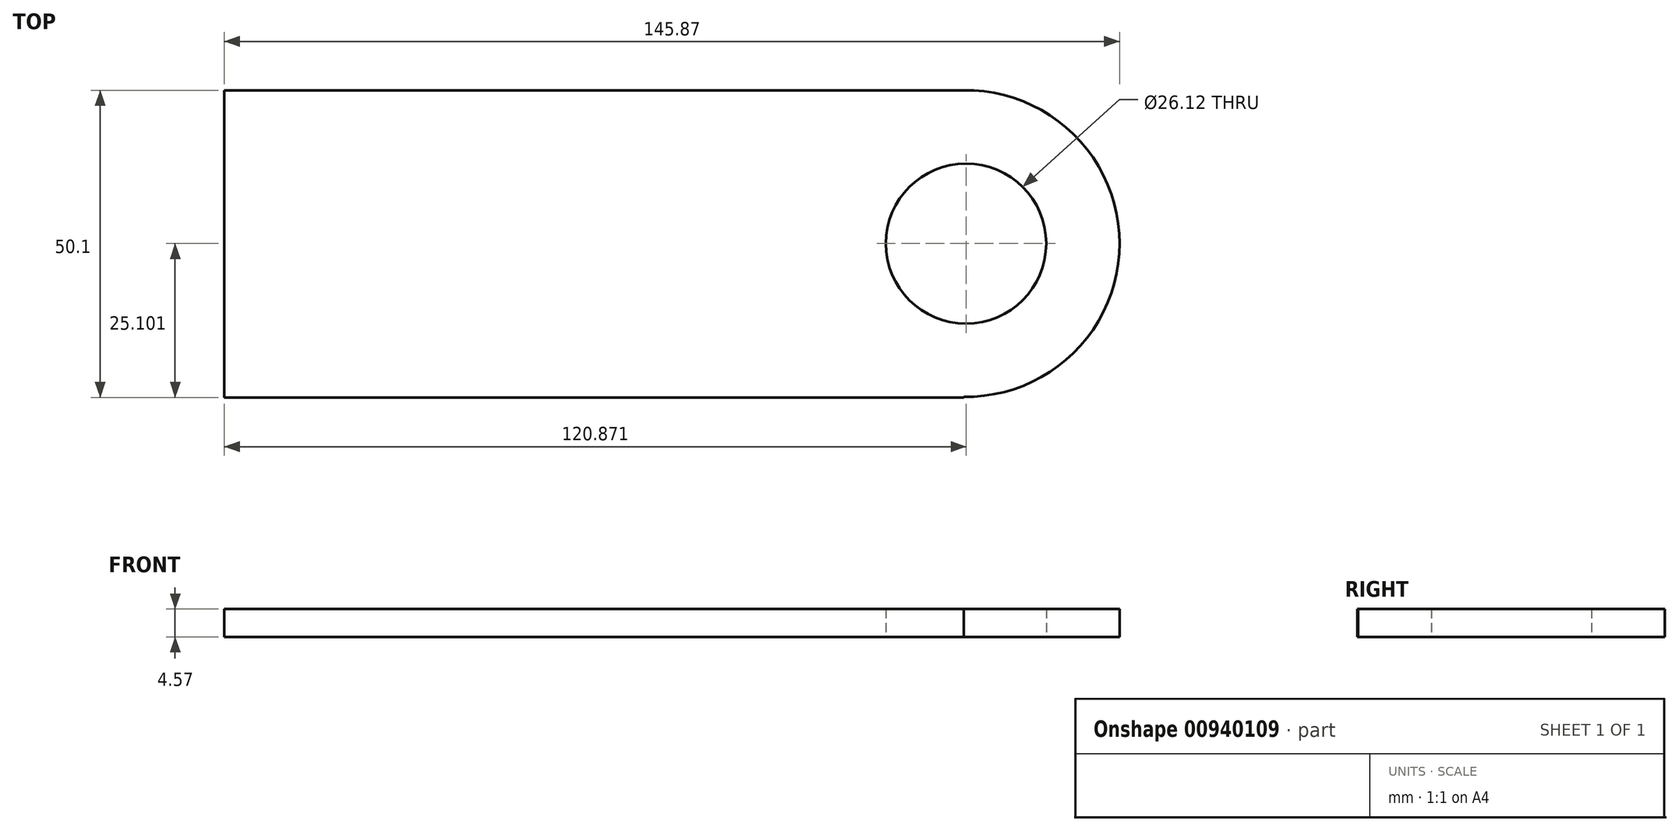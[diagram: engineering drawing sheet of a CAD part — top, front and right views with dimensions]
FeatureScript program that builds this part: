
annotation { "Feature Type Name" : "Feature", "Feature Type Description" : "" }
export const myFeature = defineFeature(function(context is Context, id is Id, definition is map)
    precondition{}
    {
        {
            var Q0;
            Q0=qCreatedBy(makeId("Top.planeOp"),FACE);
            var sketch = newSketch(context, id + "F0", { "sketchPlane" : qUnion([Q0])});
            skCircle(sketch, "E0", {"center": v(-9.74, 47.99) * mm, "radius": 25 * mm});
            skLineSegment(sketch, "E1.bottom", {"start": v(-34.74, 47.59) * mm, "end": v(15.36, 47.59) * mm});
            skLineSegment(sketch, "E1.top", {"start": v(-34.74, -72.88) * mm, "end": v(15.36, -72.88) * mm});
            skLineSegment(sketch, "E1.left", {"start": v(-34.74, 47.59) * mm, "end": v(-34.74, -72.88) * mm});
            skLineSegment(sketch, "E1.right", {"start": v(15.36, 47.59) * mm, "end": v(15.36, -72.88) * mm});
            skCircle(sketch, "E2", {"center": v(-9.74, 47.99) * mm, "radius": 13.06 * mm});
            skSolve(sketch);
        }
        {
            var Q0;
            Q0 = qSketchRegion(id + "F0", true);
            extrude(context, id + "F1", {"entities" : qUnion([Q0]), "depth" : 4.57 * mm, "offsetDistance" : 25.4 * mm});
        }
        {
            var Q0;
            Q0=makeQuery(id+"F1.opExtrude","SWEPT_BODY",BODY,{"disambiguationData":[OSD([sQuery(id+"F0.wireOp",EDGE,"E0"),sQuery(id+"F0.wireOp",EDGE,"E1.bottom"),sQuery(id+"F0.wireOp",EDGE,"E1.top"),sQuery(id+"F0.wireOp",EDGE,"E1.left"),sQuery(id+"F0.wireOp",EDGE,"E1.right"),sQuery(id+"F0.wireOp",EDGE,"E2")])]});
            var Q1;
            Q1=makeQuery(id+"F1.opExtrude","SWEPT_EDGE",EDGE,{"disambiguationData":[OSD([sQuery(id+"F0.wireOp",EDGE,"E0"),sQuery(id+"F0.wireOp",EDGE,"E1.bottom"),sQuery(id+"F0.wireOp",EDGE,"E1.left")])]});
            transform(context, id + "F2", {"entities" : qUnion([Q0]), "transformType" : TransformType.ROTATION, "transformAxis" : qUnion([Q1]), "angle" : 90 * degree, "makeCopy" : false});
        }
    });
